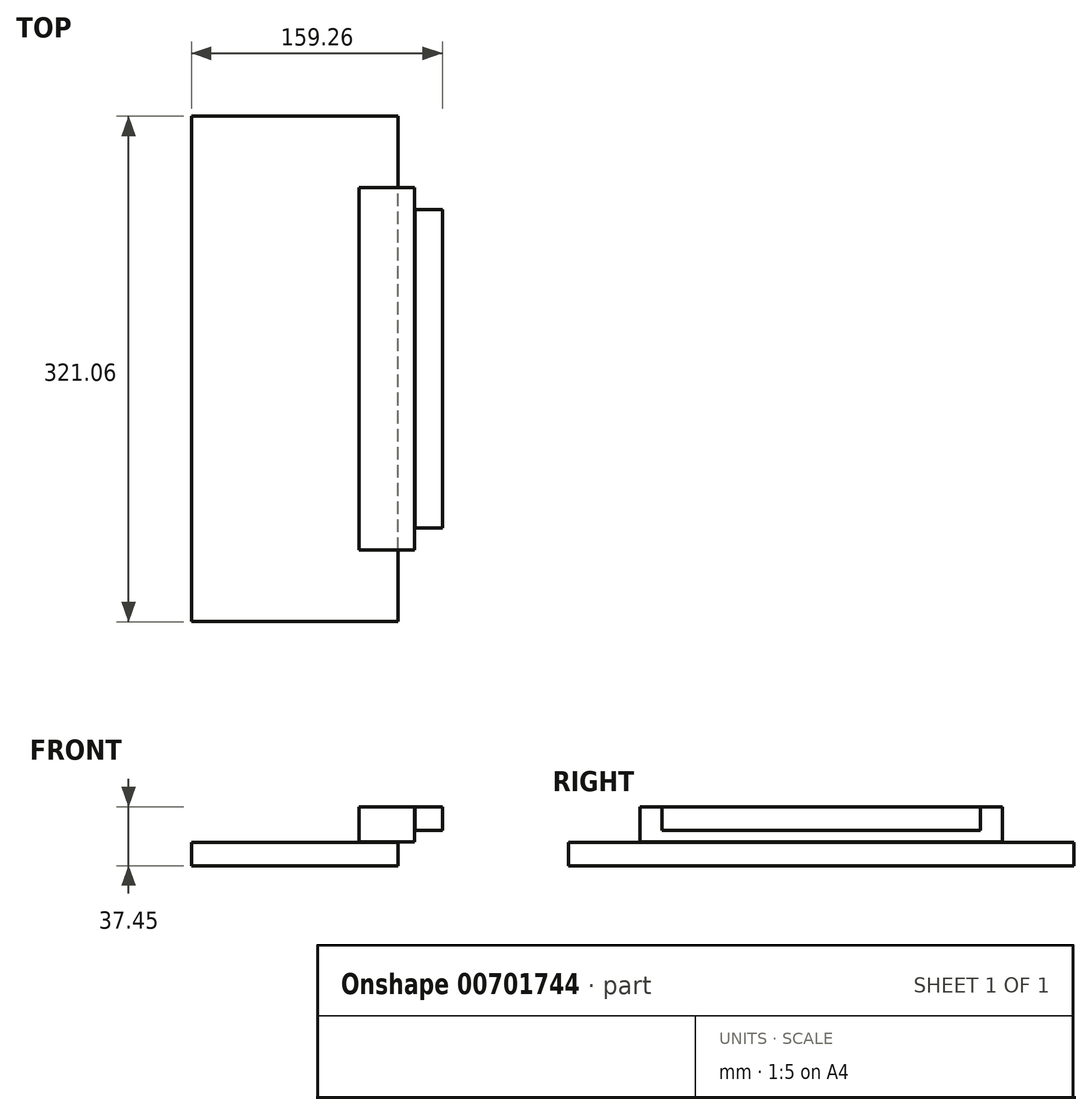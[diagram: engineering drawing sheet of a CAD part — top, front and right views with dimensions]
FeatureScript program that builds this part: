
annotation { "Feature Type Name" : "Feature", "Feature Type Description" : "" }
export const myFeature = defineFeature(function(context is Context, id is Id, definition is map)
    precondition{}
    {
        {
            var Q0;
            Q0=qCreatedBy(makeId("Front.planeOp"),FACE);
            var sketch = newSketch(context, id + "F0", { "sketchPlane" : qUnion([Q0])});
            skLineSegment(sketch, "E0.bottom", {"start": v(-65.39, 7.64) * mm, "end": v(65.76, 7.64) * mm});
            skLineSegment(sketch, "E0.top", {"start": v(-65.39, -7.08) * mm, "end": v(65.76, -7.08) * mm});
            skLineSegment(sketch, "E0.left", {"start": v(-65.39, 7.64) * mm, "end": v(-65.39, -7.08) * mm});
            skLineSegment(sketch, "E0.right", {"start": v(65.76, 7.64) * mm, "end": v(65.76, -7.08) * mm});
            skSolve(sketch);
        }
        {
            var Q0;
            Q0=qCreatedBy(makeId("Front.planeOp"),FACE);
            var sketch = newSketch(context, id + "F1", { "sketchPlane" : qUnion([Q0])});
            skLineSegment(sketch, "E1.bottom", {"start": v(41.04, 30.29) * mm, "end": v(76.33, 30.29) * mm});
            skLineSegment(sketch, "E1.top", {"start": v(41.04, 8.02) * mm, "end": v(76.33, 8.02) * mm});
            skLineSegment(sketch, "E1.left", {"start": v(41.04, 30.29) * mm, "end": v(41.04, 8.02) * mm});
            skLineSegment(sketch, "E1.right", {"start": v(76.33, 30.29) * mm, "end": v(76.33, 8.02) * mm});
            skSolve(sketch);
        }
        {
            var Q0;
            Q0=qCreatedBy(makeId("Front.planeOp"),FACE);
            var sketch = newSketch(context, id + "F2", { "sketchPlane" : qUnion([Q0])});
            skLineSegment(sketch, "E2.bottom", {"start": v(76.42, 30.37) * mm, "end": v(93.87, 30.37) * mm});
            skLineSegment(sketch, "E2.top", {"start": v(76.42, 15.3) * mm, "end": v(93.87, 15.3) * mm});
            skLineSegment(sketch, "E2.left", {"start": v(76.42, 30.37) * mm, "end": v(76.42, 15.3) * mm});
            skLineSegment(sketch, "E2.right", {"start": v(93.87, 30.37) * mm, "end": v(93.87, 15.3) * mm});
            skSolve(sketch);
        }
        {
            var Q0;
            Q0=qCreatedBy(makeId("Front.planeOp"),FACE);
            var sketch = newSketch(context, id + "F3", { "sketchPlane" : qUnion([Q0])});
            skArc(sketch, "E3", {"start": v(41.02, 30.4) * mm, "mid": v(-15.18, 33.4) * mm, "end": v(-65.29, 7.8) * mm});
            skSolve(sketch);
        }
        {
            var Q0;
            Q0 = qSketchRegion(id + "F3", true);
            var Q1;
            Q1=makeQuery(id+"F0.imprint","IMPRINT",FACE,{"disambiguationData":[TD([[makeQuery(id+"F0.imprint","IMPRINT",EDGE,{"derivedFrom":sQuery(id+"F0.wireOp",EDGE,"E0.bottom")}),-1.0]])]});
            extrude(context, id + "F4", {"entities" : qUnion([Q0, Q1]), "endBound" : BoundingType.SYMMETRIC, "depth" : 321.06 * mm, "offsetDistance" : 25.4 * mm});
        }
        {
            var Q0;
            Q0=makeQuery(id+"F1.imprint","IMPRINT",FACE,{"disambiguationData":[TD([[makeQuery(id+"F1.imprint","IMPRINT",EDGE,{"derivedFrom":sQuery(id+"F1.wireOp",EDGE,"E1.bottom")}),-1.0]])]});
            extrude(context, id + "F5", {"entities" : qUnion([Q0]), "endBound" : BoundingType.SYMMETRIC, "depth" : 230.12 * mm, "offsetDistance" : 25.4 * mm});
        }
        {
            var Q0;
            Q0=makeQuery(id+"F2.imprint","IMPRINT",FACE,{"disambiguationData":[TD([[makeQuery(id+"F2.imprint","IMPRINT",EDGE,{"derivedFrom":sQuery(id+"F2.wireOp",EDGE,"E2.bottom")}),-1.0]])]});
            var sketch = newSketch(context, id + "F6", { "sketchPlane" : qUnion([Q0])});
            skSolve(sketch);
        }
        {
            var Q0;
            Q0=makeQuery(id+"F6.imprint","IMPRINT",FACE,{"disambiguationData":[TD([[makeQuery(id+"F6.imprint","IMPRINT",EDGE,{"derivedFrom":makeQuery(id+"F2.imprint","IMPRINT",EDGE,{"derivedFrom":sQuery(id+"F2.wireOp",EDGE,"E2.bottom")})}),-1.0]])]});
            extrude(context, id + "F7", {"entities" : qUnion([Q0]), "endBound" : BoundingType.SYMMETRIC, "depth" : 202.18 * mm, "offsetDistance" : 25.4 * mm});
        }
    });
